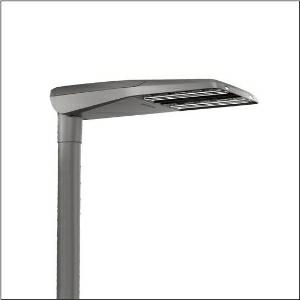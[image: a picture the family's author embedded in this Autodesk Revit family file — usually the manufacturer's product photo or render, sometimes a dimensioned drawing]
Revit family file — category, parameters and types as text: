
# Revit family: streetlight_sl_11_iq_midi___st1_2a_5xc3a61g08me_c756
name_source: partatom
category: Lighting Fixtures
units: mm (PartAtom-declared; Revit-internal decimal feet)

## family parameters
Cut with Voids When Loaded = No
Host = Face
Light Source = No
Part Type = Normal
Room Calculation Point = No
Round Connector Dimension = Use Diameter
Shared = No

## types (1)
- --- (1 x LED, 16120 lm, 123.9 W, 2700K)
    Apparent Load = 124 VA
    CIE Flux Codes = 32 70 96 100 100
    Color Rendering = 70
    Color Temperature = 2700K
    Default Elevation = 1800 mm
    Description = Streetlight SL 11 iQ midi, mast luminaire, primary light control with 3 zone facetted reflector, of plastic, silver coated, highly specular, primary optical cover: cover, of PMMA, transparent, light distribution: ST1.2a, light emission: direct distribution, primary light characteristic: asymmetric, installation type: post-top, side-entry, lamps: LED, High Power LED, rated values: 16.120lm | 123,9W | 130,1lm/W (begin service life); end service life: 16.120lm | 130,9W; at 50% lumin. flux: 8.060lm | 56,7W | 142,2lm/W, colour temperature: 2700K, colour rendering: CRI > 70, light colour: 727, light setting 1 begin service life: 100% | 16.120lm | 123,9W | 130,1lm/W | 2.700K, light setting 1 end service life: 130,9W, further light settings possible, control: Street-Remote, Auto-Match, Temp-Guard, Lumen-Switch, Night-Set, Smart-Wire, Light-Fading, Desk-Remote (wireless, voltage-free reading and setting of iQ features in the workshop via application-optimized NFC function/RFID function), optimised constant luminous flux control (CLO 2.0), pre-setting: linear dimming characteristic, with cable H07RN-F 5x 1.5mm², mains connection: 230..240V, AC, 50/60Hz, connection cable pre-assembled, cable length: 12,5m, luminaire housing, of diecast aluminium, powder-coated, Siteco® metallic grey (DB 702S), please order mast flange separately, inclination adjustable without tools: 0°, 5°, 10°, 15° (post-top) | 0°, -5°, -10°, -15° (side-entry), sealing non-destructively replaceable, multi-level sealing system, length: 780mm, width: 376mm, height: 118mm, mast flange for spigot size: 42mm (side-entry): 5XC10008XM4, 60/48mm (side-entry/post-top): 5XC10108XM2, 76/60mm (side-entry/post-top): 5XC10108XM1, equipment: Power, protection rating (complete): IP66, insulation class (complete): insulation class II (safety insulation), certification: CE, ENEC, ENEC+, VDE, impact resistance: IK10, permissible operating ambient temperature for outdoor applications: -25..+50°C, standard-compliant lighting for roads and squares, Environmental Product Declaration (EPD) tested and certified by an independent institute, packaging unit: 1 piece

Light Distribution: ST1.2a
    Height = 118 mm
    Lamp = 1 x LED
    Lamp Light Flux = 16120 lm
    Lamp Power = 123.9 W
    Lamp count = 1
    Length = 780 mm
    Luminous efficacy = 130 lm/W
    Manufacturer = Siteco
    ModVariant = No
    Model = 5XC3A61G08ME
    Number of Poles = 1
    OnlyDefault = Yes
    Power Factor = 1
    Product Name = Streetlight SL 11 iQ midi | ST1.2a
    Product group = mast luminaire | pylon top
    ProductGroupID = 6100
    Protection Class = Protection class II
    Protection Degree = IP 66
    RLX_Detail_Level = 1
    RLX_Emergency_Light_Flux = 0 lm
    RLX_Emergency_Type = 0
    RLX_Emergency_Type_DB = No
    RlxData = <blob elided: 71029 chars, md5=1b1880ab>
    Socket = socket
    Standby Power = 0 W
    System Light Flux = 16119 lm
    System Power = 124 W
    Type Comments = factory setting: luminous flux: 100 % | dim-lin: 254 | 554 mA
    Type Image = l_1005960.jpg
    URL = http://relux.com
    VarID = @adj_078264
    Voltage = 0 V
    Weight = 0.00 kg
    Width = 376 mm

## geometry (parser evidence)
native form markers: Blend x4, Sweep x12
no freeform markers — native parametric forms only
